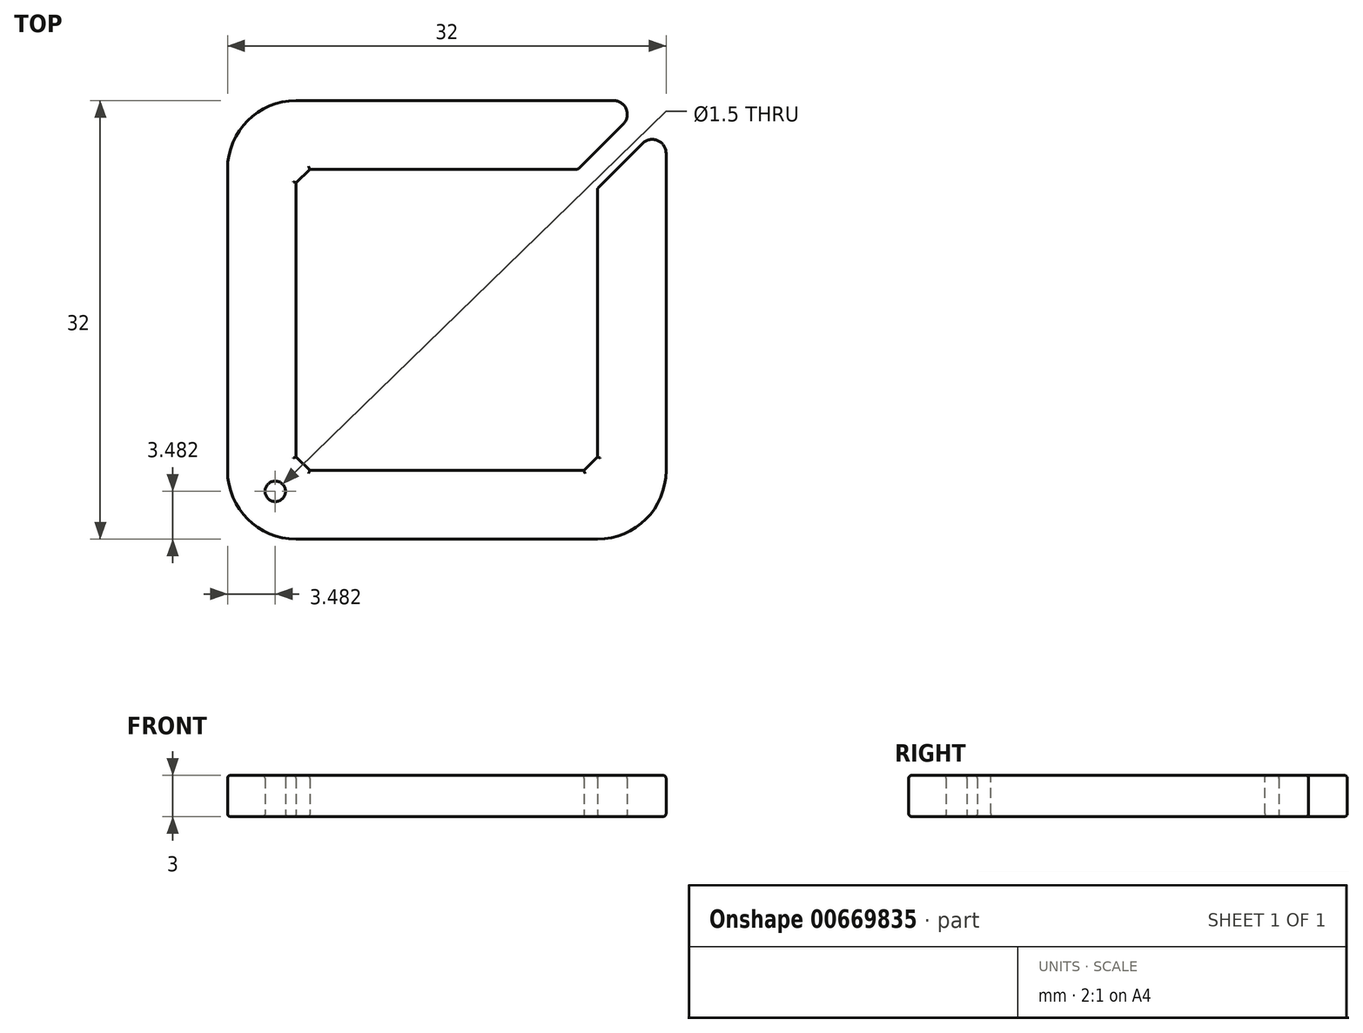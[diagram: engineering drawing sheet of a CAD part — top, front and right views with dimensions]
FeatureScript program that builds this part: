
annotation { "Feature Type Name" : "Feature", "Feature Type Description" : "" }
export const myFeature = defineFeature(function(context is Context, id is Id, definition is map)
    precondition{}
    {
        {
            var Q0;
            Q0=qCreatedBy(makeId("Top.planeOp"),FACE);
            var sketch = newSketch(context, id + "F0", { "sketchPlane" : qUnion([Q0])});
            skLineSegment(sketch, "E0.bottom", {"start": v(-16, 16) * mm, "end": v(11.15, 16) * mm});
            skLineSegment(sketch, "E0.top", {"start": v(-16, -16) * mm, "end": v(16, -16) * mm});
            skLineSegment(sketch, "E0.left", {"start": v(-16, 16) * mm, "end": v(-16, -16) * mm});
            skLineSegment(sketch, "E0.right", {"start": v(16, 11.15) * mm, "end": v(16, -16) * mm});
            skPoint(sketch, "E0.middle", {"position": v(0, 0) * mm});
            skLineSegment(sketch, "E1.bottom", {"start": v(-11, 11) * mm, "end": v(6.15, 11) * mm});
            skLineSegment(sketch, "E1.top", {"start": v(-11, -11) * mm, "end": v(11, -11) * mm});
            skLineSegment(sketch, "E1.left", {"start": v(-11, 11) * mm, "end": v(-11, -11) * mm});
            skLineSegment(sketch, "E1.right", {"start": v(11, 6.15) * mm, "end": v(11, -11) * mm});
            skLineSegment(sketch, "E2", {"start": v(14.59, 16) * mm, "end": v(9.59, 11) * mm});
            skLineSegment(sketch, "E3", {"start": v(6.15, 11) * mm, "end": v(9.59, 11) * mm});
            skLineSegment(sketch, "E4", {"start": v(11.15, 16) * mm, "end": v(14.59, 16) * mm});
            skLineSegment(sketch, "E5", {"start": v(16, 14.59) * mm, "end": v(11, 9.59) * mm});
            skLineSegment(sketch, "E6", {"start": v(11, 6.15) * mm, "end": v(11, 9.59) * mm});
            skLineSegment(sketch, "E7", {"start": v(16, 11.15) * mm, "end": v(16, 14.59) * mm});
            skCircle(sketch, "E8", {"center": v(-12.52, -12.52) * mm, "radius": 0.75 * mm});
            skSolve(sketch);
        }
        {
            var Q0;
            Q0=makeQuery(id+"F0.imprint","IMPRINT",FACE,{"disambiguationData":[TD([[makeQuery(id+"F0.imprint","IMPRINT",EDGE,{"derivedFrom":sQuery(id+"F0.wireOp",EDGE,"E0.bottom")}),-1.0]])]});
            extrude(context, id + "F1", {"entities" : qUnion([Q0]), "depth" : 3 * mm, "offsetDistance" : 25 * mm});
        }
        {
            var Q0;
            Q0=makeQuery(id+"F1.opExtrude","SWEPT_EDGE",EDGE,{"disambiguationData":[OSD([sQuery(id+"F0.wireOp",EDGE,"E1.bottom"),sQuery(id+"F0.wireOp",EDGE,"E1.left")])]});
            var Q1;
            Q1=makeQuery(id+"F1.opExtrude","SWEPT_EDGE",EDGE,{"disambiguationData":[OSD([sQuery(id+"F0.wireOp",EDGE,"E1.top"),sQuery(id+"F0.wireOp",EDGE,"E1.right")])]});
            var Q2;
            Q2=makeQuery(id+"F1.opExtrude","SWEPT_EDGE",EDGE,{"disambiguationData":[OSD([sQuery(id+"F0.wireOp",EDGE,"E1.top"),sQuery(id+"F0.wireOp",EDGE,"E1.left")])]});
            chamfer(context, id + "F2", {"entities" : qUnion([Q0, Q1, Q2]), "chamferType" : ChamferType.TWO_OFFSETS, "width1" : 1 * mm, "oppositeDirection" : false, "width2" : 1 * mm, "tangentPropagation" : true});
        }
        {
            var Q0;
            Q0=makeQuery(id+"F1.opExtrude","SWEPT_EDGE",EDGE,{"disambiguationData":[OSD([sQuery(id+"F0.wireOp",EDGE,"E0.top"),sQuery(id+"F0.wireOp",EDGE,"E0.right")])]});
            var Q1;
            Q1=makeQuery(id+"F1.opExtrude","SWEPT_EDGE",EDGE,{"disambiguationData":[OSD([sQuery(id+"F0.wireOp",EDGE,"E0.bottom"),sQuery(id+"F0.wireOp",EDGE,"E0.left")])]});
            var Q2;
            Q2=makeQuery(id+"F1.opExtrude","SWEPT_EDGE",EDGE,{"disambiguationData":[OSD([sQuery(id+"F0.wireOp",EDGE,"E0.top"),sQuery(id+"F0.wireOp",EDGE,"E0.left")])]});
            fillet(context, id + "F3", {"entities" : qUnion([Q0, Q1, Q2]), "radius" : 5 * mm, "tangentPropagation" : true, "allowEdgeOverflow" : false});
        }
        {
            var Q0;
            Q0=makeQuery(id+"F1.opExtrude","SWEPT_EDGE",EDGE,{"disambiguationData":[OSD([sQuery(id+"F0.wireOp",EDGE,"E5"),sQuery(id+"F0.wireOp",EDGE,"E7")])]});
            var Q1;
            Q1=makeQuery(id+"F1.opExtrude","SWEPT_EDGE",EDGE,{"disambiguationData":[OSD([sQuery(id+"F0.wireOp",EDGE,"E2"),sQuery(id+"F0.wireOp",EDGE,"E4")])]});
            fillet(context, id + "F4", {"entities" : qUnion([Q0, Q1]), "radius" : 1 * mm, "tangentPropagation" : true, "allowEdgeOverflow" : false});
        }
        {
            var Q0;
            Q0=makeQuery(id+"F1.opExtrude","CAP_EDGE",EDGE,{"disambiguationData":[OSD([sQuery(id+"F0.wireOp",EDGE,"E0.right"),sQuery(id+"F0.wireOp",EDGE,"E7")])],"isStart":false});
            var Q1;
            Q1=makeQuery(id+"F1.opExtrude","CAP_EDGE",EDGE,{"disambiguationData":[OSD([sQuery(id+"F0.wireOp",EDGE,"E0.right"),sQuery(id+"F0.wireOp",EDGE,"E7")])],"isStart":true});
            var Q2;
            Q2=makeQuery(id+"F1.opExtrude","CAP_FACE",FACE,{"disambiguationData":[OSD([sQuery(id+"F0.wireOp",EDGE,"E0.bottom"),sQuery(id+"F0.wireOp",EDGE,"E0.top"),sQuery(id+"F0.wireOp",EDGE,"E0.left"),sQuery(id+"F0.wireOp",EDGE,"E0.right"),sQuery(id+"F0.wireOp",EDGE,"E1.bottom"),sQuery(id+"F0.wireOp",EDGE,"E1.top"),sQuery(id+"F0.wireOp",EDGE,"E1.left"),sQuery(id+"F0.wireOp",EDGE,"E1.right"),sQuery(id+"F0.wireOp",EDGE,"E2"),sQuery(id+"F0.wireOp",EDGE,"E3"),sQuery(id+"F0.wireOp",EDGE,"E4"),sQuery(id+"F0.wireOp",EDGE,"E5"),sQuery(id+"F0.wireOp",EDGE,"E6"),sQuery(id+"F0.wireOp",EDGE,"E7"),sQuery(id+"F0.wireOp",EDGE,"E8")])],"isStart":false});
            var Q3;
            Q3=makeQuery(id+"F1.opExtrude","CAP_FACE",FACE,{"disambiguationData":[OSD([sQuery(id+"F0.wireOp",EDGE,"E0.bottom"),sQuery(id+"F0.wireOp",EDGE,"E0.top"),sQuery(id+"F0.wireOp",EDGE,"E0.left"),sQuery(id+"F0.wireOp",EDGE,"E0.right"),sQuery(id+"F0.wireOp",EDGE,"E1.bottom"),sQuery(id+"F0.wireOp",EDGE,"E1.top"),sQuery(id+"F0.wireOp",EDGE,"E1.left"),sQuery(id+"F0.wireOp",EDGE,"E1.right"),sQuery(id+"F0.wireOp",EDGE,"E2"),sQuery(id+"F0.wireOp",EDGE,"E3"),sQuery(id+"F0.wireOp",EDGE,"E4"),sQuery(id+"F0.wireOp",EDGE,"E5"),sQuery(id+"F0.wireOp",EDGE,"E6"),sQuery(id+"F0.wireOp",EDGE,"E7"),sQuery(id+"F0.wireOp",EDGE,"E8")])],"isStart":true});
            var Q4;
            Q4=makeQuery(id+"F1.opExtrude","SWEPT_EDGE",EDGE,{"disambiguationData":[OSD([sQuery(id+"F0.wireOp",EDGE,"E5"),sQuery(id+"F0.wireOp",EDGE,"E6")])]});
            var Q5;
            Q5=makeQuery(id+"F1.opExtrude","SWEPT_EDGE",EDGE,{"disambiguationData":[OSD([sQuery(id+"F0.wireOp",EDGE,"E2"),sQuery(id+"F0.wireOp",EDGE,"E3")])]});
            fillet(context, id + "F5", {"entities" : qUnion([Q0, Q1, Q2, Q3, Q4, Q5]), "tangentPropagation" : true, "radius" : 0.2 * mm, "defaultsChanged" : false, "vertexSettings" : [], "allowEdgeOverflow" : false});
        }
    });
